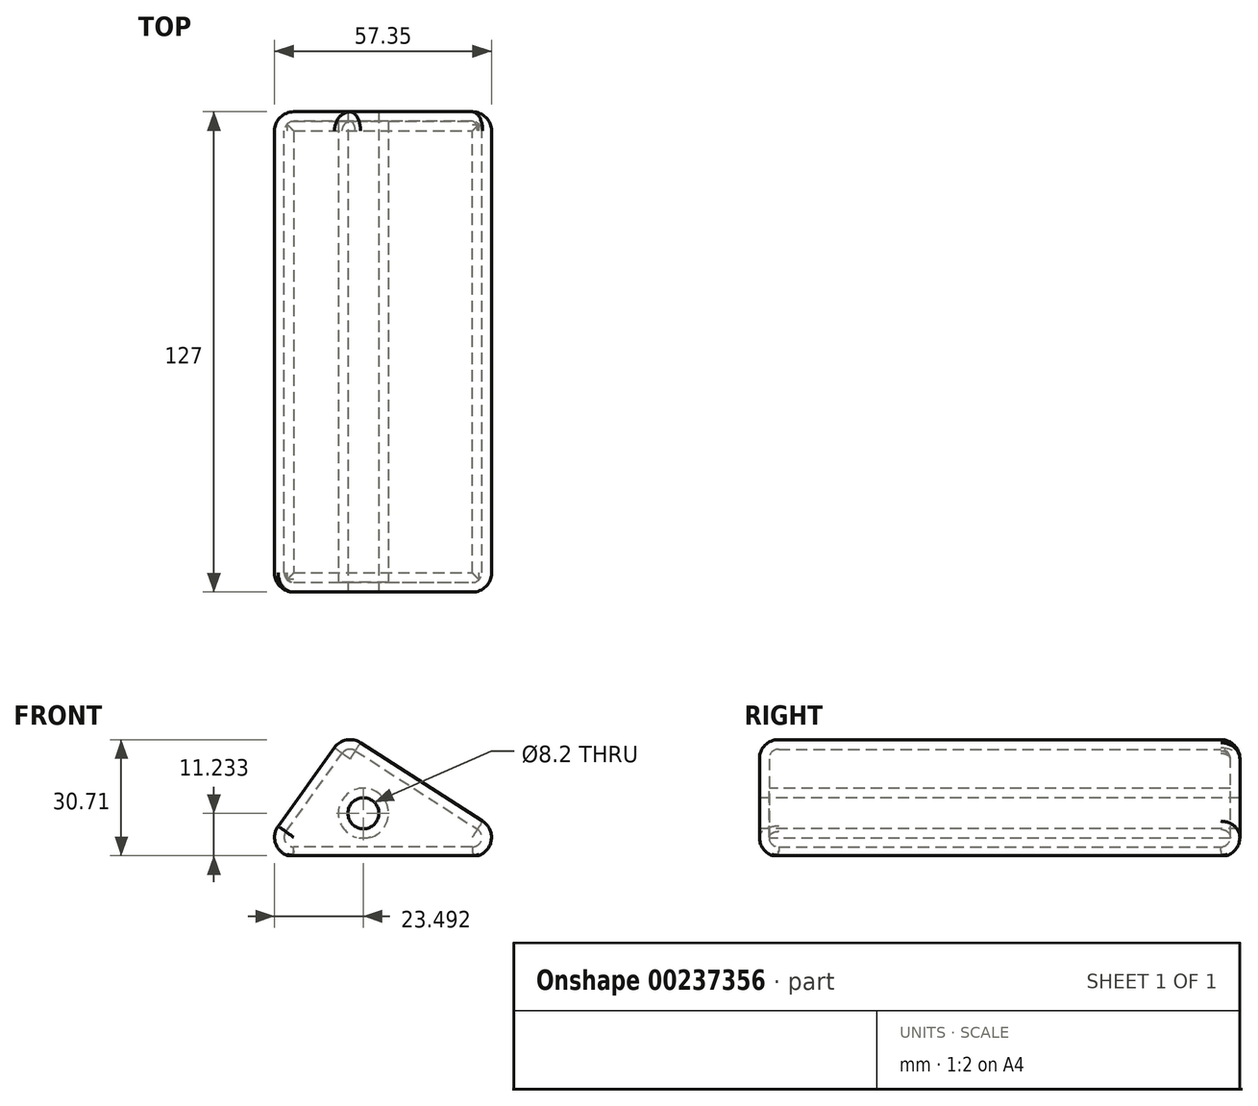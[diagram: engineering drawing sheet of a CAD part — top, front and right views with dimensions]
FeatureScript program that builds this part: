
annotation { "Feature Type Name" : "Feature", "Feature Type Description" : "" }
export const myFeature = defineFeature(function(context is Context, id is Id, definition is map)
    precondition{}
    {
        {
            var Q0;
            Q0=qCreatedBy(makeId("Front.planeOp"),FACE);
            var sketch = newSketch(context, id + "F0", { "sketchPlane" : qUnion([Q0])});
            skLineSegment(sketch, "E0", {"start": v(0, 0) * mm, "end": v(23.48, 32.73) * mm});
            skLineSegment(sketch, "E1", {"start": v(23.48, 32.73) * mm, "end": v(23.48, 32.73) * mm});
            skLineSegment(sketch, "E2", {"start": v(74.37, 0) * mm, "end": v(0, 0) * mm});
            skLineSegment(sketch, "E3", {"start": v(23.48, 32.73) * mm, "end": v(74.37, 0) * mm});
            skSolve(sketch);
        }
        {
            var Q0;
            Q0=qSketchRegion(id+"F0",true);
            extrude(context, id + "F1", {"entities" : qUnion([Q0]), "depth" : 127 * mm});
        }
        {
            var Q0;
            Q0=makeQuery(id+"F1.opExtrude","CAP_EDGE",EDGE,{"disambiguationData":[OSD([sQuery(id+"F0.wireOp",EDGE,"E3")])],"isStart":false});
            var Q1;
            Q1=makeQuery(id+"F1.opExtrude","SWEPT_EDGE",EDGE,{"disambiguationData":[OSD([sQuery(id+"F0.wireOp",EDGE,"E0"),sQuery(id+"F0.wireOp",EDGE,"E3")])]});
            var Q2;
            Q2=makeQuery(id+"F1.opExtrude","CAP_EDGE",EDGE,{"disambiguationData":[OSD([sQuery(id+"F0.wireOp",EDGE,"E3")])],"isStart":true});
            var Q3;
            Q3=makeQuery(id+"F1.opExtrude","SWEPT_EDGE",EDGE,{"disambiguationData":[OSD([sQuery(id+"F0.wireOp",EDGE,"E2"),sQuery(id+"F0.wireOp",EDGE,"E3")])]});
            var Q4;
            Q4=makeQuery(id+"F1.opExtrude","CAP_EDGE",EDGE,{"disambiguationData":[OSD([sQuery(id+"F0.wireOp",EDGE,"E2")])],"isStart":false});
            var Q5;
            Q5=makeQuery(id+"F1.opExtrude","CAP_EDGE",EDGE,{"disambiguationData":[OSD([sQuery(id+"F0.wireOp",EDGE,"E0")])],"isStart":false});
            fillet(context, id + "F6", {"entities" : qUnion([Q0, Q1, Q2, Q3, Q4, Q5]), "radius" : 5.08 * mm, "tangentPropagation" : true, "allowEdgeOverflow" : false});
        }
        {
            var Q0;
            Q0=makeQuery(id+"F1.opExtrude","SWEPT_FACE",FACE,{"disambiguationData":[OSD([sQuery(id+"F0.wireOp",EDGE,"E3")])]});
            var Q1;
            Q1=makeQuery(id+"F1.opExtrude","SWEPT_EDGE",EDGE,{"disambiguationData":[OSD([sQuery(id+"F0.wireOp",EDGE,"E0"),sQuery(id+"F0.wireOp",EDGE,"E2")])]});
            var Q2;
            Q2=makeQuery(id+"F1.opExtrude","CAP_EDGE",EDGE,{"disambiguationData":[OSD([sQuery(id+"F0.wireOp",EDGE,"E0")])],"isStart":true});
            var Q3;
            Q3=makeQuery(id+"F1.opExtrude","CAP_EDGE",EDGE,{"disambiguationData":[OSD([sQuery(id+"F0.wireOp",EDGE,"E2")])],"isStart":true});
            fillet(context, id + "F7", {"entities" : qUnion([Q0, Q1, Q2, Q3]), "radius" : 5.08 * mm, "tangentPropagation" : true, "allowEdgeOverflow" : false});
        }
        {
            var Q0;
            Q0=makeQuery(id+"F1.opExtrude","CAP_FACE",FACE,{"disambiguationData":[OSD([sQuery(id+"F0.wireOp",EDGE,"E0"),sQuery(id+"F0.wireOp",EDGE,"E2"),sQuery(id+"F0.wireOp",EDGE,"E3")])],"isStart":false});
            var sketch = newSketch(context, id + "F2", { "sketchPlane" : qUnion([Q0])});
            skCircle(sketch, "E4", {"center": v(28.3, 11.45) * mm, "radius": 4.1 * mm});
            skSolve(sketch);
        }
        {
            var Q0;
            Q0=makeQuery(id+"F2.imprint","IMPRINT",FACE,{"disambiguationData":[TD([[makeQuery(id+"F2.imprint","IMPRINT",EDGE,{"derivedFrom":sQuery(id+"F2.wireOp",EDGE,"E4")}),1.0]])]});
            extrude(context, id + "F3", {"entities" : qUnion([Q0]), "operationType" : NewBodyOperationType.REMOVE, "endBound" : BoundingType.THROUGH_ALL, "oppositeDirection" : true, "depth" : 25.4 * mm});
        }
        {
            var Q0;
            Q0=makeQuery(id+"F1.opExtrude","SWEPT_FACE",FACE,{"disambiguationData":[OSD([sQuery(id+"F0.wireOp",EDGE,"E2")])]});
            shell(context, id + "F4", {"entities" : qUnion([Q0]), "thickness" : 2.54 * mm});
        }
        {
            var Q0;
            {var subQ0=sQuery(id+"F0.wireOp",EDGE,"E2");Q0=makeQuery(id+"F6.opFillet","BLEND_EDGE",EDGE,{"blendedFrom":[makeQuery(id+"F1.opExtrude","SWEPT_EDGE",EDGE,{"disambiguationData":[OSD([subQ0,sQuery(id+"F0.wireOp",EDGE,"E3")])]}),makeQuery(id+"F1.opExtrude","SWEPT_FACE",FACE,{"disambiguationData":[OSD([subQ0])]})],"blendedInto":[makeQuery(id+"F1.opExtrude","SWEPT_FACE",FACE,{"disambiguationData":[OSD([subQ0])]})]});}
            var Q1;
            {var subQ0=sQuery(id+"F0.wireOp",EDGE,"E2");Q1=makeQuery(id+"F7.opFillet","BLEND_EDGE",EDGE,{"blendedFrom":[makeQuery(id+"F1.opExtrude","CAP_EDGE",EDGE,{"disambiguationData":[OSD([subQ0])],"isStart":true}),makeQuery(id+"F1.opExtrude","SWEPT_FACE",FACE,{"disambiguationData":[OSD([subQ0])]})],"blendedInto":[makeQuery(id+"F1.opExtrude","SWEPT_FACE",FACE,{"disambiguationData":[OSD([subQ0])]})]});}
            var Q2;
            {var subQ0=sQuery(id+"F0.wireOp",EDGE,"E2");Q2=makeQuery(id+"F7.opFillet","BLEND_EDGE",EDGE,{"blendedFrom":[makeQuery(id+"F1.opExtrude","SWEPT_EDGE",EDGE,{"disambiguationData":[OSD([sQuery(id+"F0.wireOp",EDGE,"E0"),subQ0])]}),makeQuery(id+"F1.opExtrude","SWEPT_FACE",FACE,{"disambiguationData":[OSD([subQ0])]})],"blendedInto":[makeQuery(id+"F1.opExtrude","SWEPT_FACE",FACE,{"disambiguationData":[OSD([subQ0])]})]});}
            var Q3;
            {var subQ0=sQuery(id+"F0.wireOp",EDGE,"E2");Q3=makeQuery(id+"F6.opFillet","BLEND_EDGE",EDGE,{"blendedFrom":[makeQuery(id+"F1.opExtrude","CAP_EDGE",EDGE,{"disambiguationData":[OSD([subQ0])],"isStart":false}),makeQuery(id+"F1.opExtrude","SWEPT_FACE",FACE,{"disambiguationData":[OSD([subQ0])]})],"blendedInto":[makeQuery(id+"F1.opExtrude","SWEPT_FACE",FACE,{"disambiguationData":[OSD([subQ0])]})]});}
            fillet(context, id + "F5", {"entities" : qUnion([Q0, Q1, Q2, Q3]), "radius" : 1.27 * mm, "tangentPropagation" : true, "allowEdgeOverflow" : false});
        }
    });
